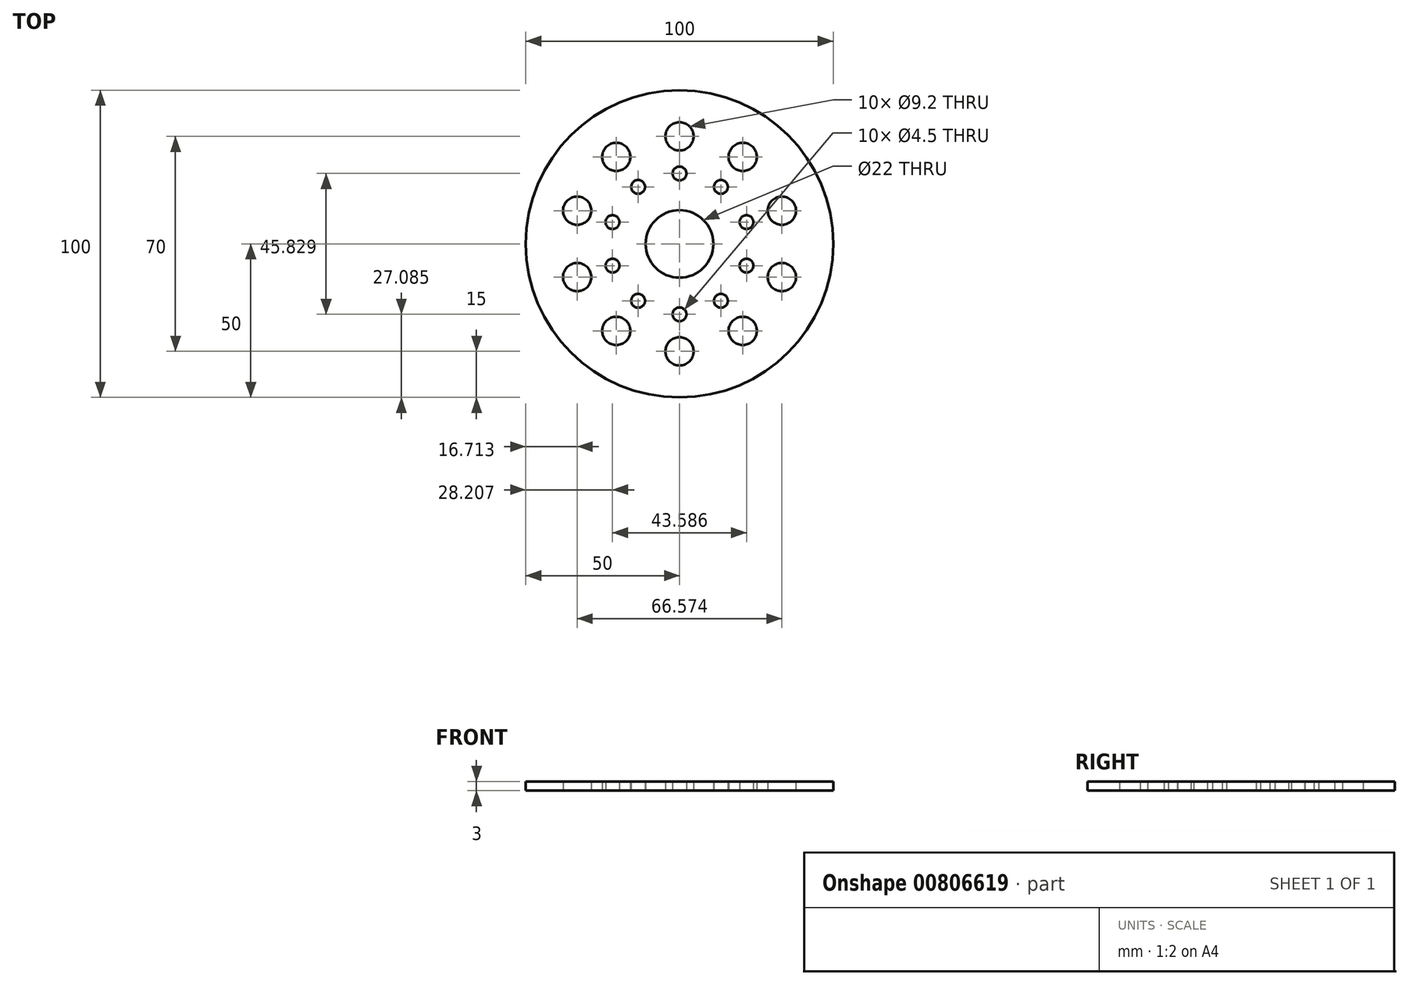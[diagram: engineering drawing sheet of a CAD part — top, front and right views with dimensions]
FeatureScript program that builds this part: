
annotation { "Feature Type Name" : "Feature", "Feature Type Description" : "" }
export const myFeature = defineFeature(function(context is Context, id is Id, definition is map)
    precondition{}
    {
        {
            var Q0;
            Q0=qCreatedBy(makeId("Top.planeOp"),FACE);
            var sketch = newSketch(context, id + "F0", { "sketchPlane" : qUnion([Q0])});
            skArc(sketch, "E0", {"start": v(15.45, 47.55) * mm, "mid": v(0, 50) * mm, "end": v(-15.45, 47.55) * mm});
            skArc(sketch, "E1", {"start": v(3.4, 10.46) * mm, "mid": v(0, 11) * mm, "end": v(-3.4, 10.46) * mm});
            skCircle(sketch, "E2", {"center": v(0, 35) * mm, "radius": 4.6 * mm});
            skCircle(sketch, "E3", {"center": v(0, 22.91) * mm, "radius": 2.25 * mm});
            skArc(sketch, "E4.1.0", {"start": v(-15.45, 47.55) * mm, "mid": v(-29.39, 40.45) * mm, "end": v(-40.45, 29.39) * mm});
            skCircle(sketch, "E4.1.1", {"center": v(-20.57, 28.32) * mm, "radius": 4.6 * mm});
            skCircle(sketch, "E4.1.2", {"center": v(-13.47, 18.54) * mm, "radius": 2.25 * mm});
            skArc(sketch, "E4.1.3", {"start": v(-3.4, 10.46) * mm, "mid": v(-6.47, 8.9) * mm, "end": v(-8.9, 6.47) * mm});
            skArc(sketch, "E4.2.0", {"start": v(-40.45, 29.39) * mm, "mid": v(-47.55, 15.45) * mm, "end": v(-50, 0) * mm});
            skCircle(sketch, "E4.2.1", {"center": v(-33.29, 10.82) * mm, "radius": 4.6 * mm});
            skCircle(sketch, "E4.2.2", {"center": v(-21.8, 7.08) * mm, "radius": 2.25 * mm});
            skArc(sketch, "E4.2.3", {"start": v(-8.9, 6.47) * mm, "mid": v(-10.46, 3.4) * mm, "end": v(-11, 0) * mm});
            skArc(sketch, "E4.3.0", {"start": v(-50, 0) * mm, "mid": v(-47.55, -15.45) * mm, "end": v(-40.45, -29.39) * mm});
            skCircle(sketch, "E4.3.1", {"center": v(-33.29, -10.82) * mm, "radius": 4.6 * mm});
            skCircle(sketch, "E4.3.2", {"center": v(-21.8, -7.08) * mm, "radius": 2.25 * mm});
            skArc(sketch, "E4.3.3", {"start": v(-11, 0) * mm, "mid": v(-10.46, -3.4) * mm, "end": v(-8.9, -6.47) * mm});
            skArc(sketch, "E4.4.0", {"start": v(-40.45, -29.39) * mm, "mid": v(-29.39, -40.45) * mm, "end": v(-15.45, -47.55) * mm});
            skCircle(sketch, "E4.4.1", {"center": v(-20.57, -28.32) * mm, "radius": 4.6 * mm});
            skCircle(sketch, "E4.4.2", {"center": v(-13.47, -18.54) * mm, "radius": 2.25 * mm});
            skArc(sketch, "E4.4.3", {"start": v(-8.9, -6.47) * mm, "mid": v(-6.47, -8.9) * mm, "end": v(-3.4, -10.46) * mm});
            skArc(sketch, "E4.5.0", {"start": v(-15.45, -47.55) * mm, "mid": v(0, -50) * mm, "end": v(15.45, -47.55) * mm});
            skCircle(sketch, "E4.5.1", {"center": v(0, -35) * mm, "radius": 4.6 * mm});
            skCircle(sketch, "E4.5.2", {"center": v(0, -22.91) * mm, "radius": 2.25 * mm});
            skArc(sketch, "E4.5.3", {"start": v(-3.4, -10.46) * mm, "mid": v(0, -11) * mm, "end": v(3.4, -10.46) * mm});
            skArc(sketch, "E4.6.0", {"start": v(15.45, -47.55) * mm, "mid": v(29.39, -40.45) * mm, "end": v(40.45, -29.39) * mm});
            skCircle(sketch, "E4.6.1", {"center": v(20.57, -28.32) * mm, "radius": 4.6 * mm});
            skCircle(sketch, "E4.6.2", {"center": v(13.47, -18.54) * mm, "radius": 2.25 * mm});
            skArc(sketch, "E4.6.3", {"start": v(3.4, -10.46) * mm, "mid": v(6.47, -8.9) * mm, "end": v(8.9, -6.47) * mm});
            skArc(sketch, "E4.7.0", {"start": v(40.45, -29.39) * mm, "mid": v(47.55, -15.45) * mm, "end": v(50, 0) * mm});
            skCircle(sketch, "E4.7.1", {"center": v(33.29, -10.82) * mm, "radius": 4.6 * mm});
            skCircle(sketch, "E4.7.2", {"center": v(21.8, -7.08) * mm, "radius": 2.25 * mm});
            skArc(sketch, "E4.7.3", {"start": v(8.9, -6.47) * mm, "mid": v(10.46, -3.4) * mm, "end": v(11, 0) * mm});
            skArc(sketch, "E4.8.0", {"start": v(50, 0) * mm, "mid": v(47.55, 15.45) * mm, "end": v(40.45, 29.39) * mm});
            skCircle(sketch, "E4.8.1", {"center": v(33.29, 10.82) * mm, "radius": 4.6 * mm});
            skCircle(sketch, "E4.8.2", {"center": v(21.8, 7.08) * mm, "radius": 2.25 * mm});
            skArc(sketch, "E4.8.3", {"start": v(11, 0) * mm, "mid": v(10.46, 3.4) * mm, "end": v(8.9, 6.47) * mm});
            skArc(sketch, "E4.9.0", {"start": v(40.45, 29.39) * mm, "mid": v(29.39, 40.45) * mm, "end": v(15.45, 47.55) * mm});
            skCircle(sketch, "E4.9.1", {"center": v(20.57, 28.32) * mm, "radius": 4.6 * mm});
            skCircle(sketch, "E4.9.2", {"center": v(13.47, 18.54) * mm, "radius": 2.25 * mm});
            skArc(sketch, "E4.9.3", {"start": v(8.9, 6.47) * mm, "mid": v(6.47, 8.9) * mm, "end": v(3.4, 10.46) * mm});
            skSolve(sketch);
        }
        {
            var Q0;
            Q0 = qSketchRegion(id + "F0", true);
            extrude(context, id + "F1", {"entities" : qUnion([Q0]), "depth" : 3 * mm, "offsetDistance" : 25 * mm});
        }
    });
